# Revit family: Bernhardt_Design-Seating-Ottomans-Elevation
name_source: partatom
category: Furniture
revit_build: Autodesk Revit 2016 (Build: 20150714_1515(x64)
units: mm (PartAtom-declared; Revit-internal decimal feet)

## family parameters
Always vertical = Yes
Cut with Voids When Loaded = No
OmniClass Number = 23.40.20.00
OmniClass Title = General Furniture and Specialties
Room Calculation Point = No
Shared = No
Work Plane-Based = No

## types (6) — shared parameters
Fabric = <By Category>
Manufacturer = Bernhardt Design
Model = Elevation
URL = http://www.bernhardtdesign.com

## per-type parameters (varying)
| type | 20A | 20AM | 21A | 21AM | 22A | 23A | CasterRadius | Casters | GlideRadius | Glides |
| Elevation 3820A | Yes | No | No | No | No | No | 0' - 8 1/16" | No | 0' - 8 1/16" | Yes |
| Elevation 3820AM | No | Yes | No | No | No | No | 0' - 8 1/16" | Yes | 0' - 8 1/16" | No |
| Elevation 3821A | No | No | Yes | No | No | No | 0' - 8 1/16" | No | 0' - 10 3/8" | Yes |
| Elevation 3821AM | No | No | No | Yes | No | No | 0' - 10 3/8" | Yes | 0' - 10 3/8" | No |
| Elevation 3822A | No | No | No | No | Yes | No | 0' - 10 3/8" | No | 1' - 0 3/4" | Yes |
| Elevation 3823A | No | No | No | No | No | Yes | 0' - 10 3/8" | No | 1' - 4 1/4" | Yes |

note: column(s) folded — value = type name in every type: Catalog, SKU

## geometry (parser evidence)
native form markers: Sweep x2
no freeform markers — native parametric forms only
